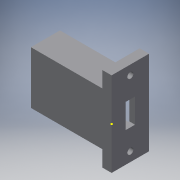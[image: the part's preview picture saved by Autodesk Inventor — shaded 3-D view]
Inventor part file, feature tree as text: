
AUTODESK INVENTOR PART (.ipt)
format: ipt  version: 2018 (Build 220112000, 112)  size: 175,616 bytes
history: native  units: mm
features: extrude x5, sketch x3
ambient origin geometry x8: Origin, YZ Plane, XZ Plane, XY Plane, X Axis, Y Axis, Z Axis, Center Point
bodies: Solid1 (feature_tree)
feature tree (8):
  extrude  "Extrusion1"  Depth=13.0mm
  extrude  "Extrusion2"  Depth=45.0mm
  sketch  "Sketch3"  dims[d0=5.0mm d1=13.0mm]
  extrude  "Extrusion5"  Depth=20.0mm
  extrude  "Extrusion8"  Depth=11.0mm
  extrude  "Extrusion10"  Depth=31.0mm TaperAngle=0.0deg
  sketch  "Sketch6"  dims[d2=20.0mm d3=45.0mm]
  sketch  "Sketch8"  dims[d4=5.0mm d5=0.0mm d6=20.0mm d7=11.0mm d9=31.0mm d10=0.0mm d11=12.0mm d12=11.0mm d17=5.0mm d18=3.2mm d19=3.2mm d20=5.0mm d21=3.2mm d22=3.2mm d23=5.0mm d24=5.0mm d25=5.0mm d26=0.0mm d27=4.5mm d32=14.0mm d33=14.0mm d34=7.0mm d35=0.0mm d36=12.0mm d39=2.0mm d40=0.0mm d41=10.0mm]
